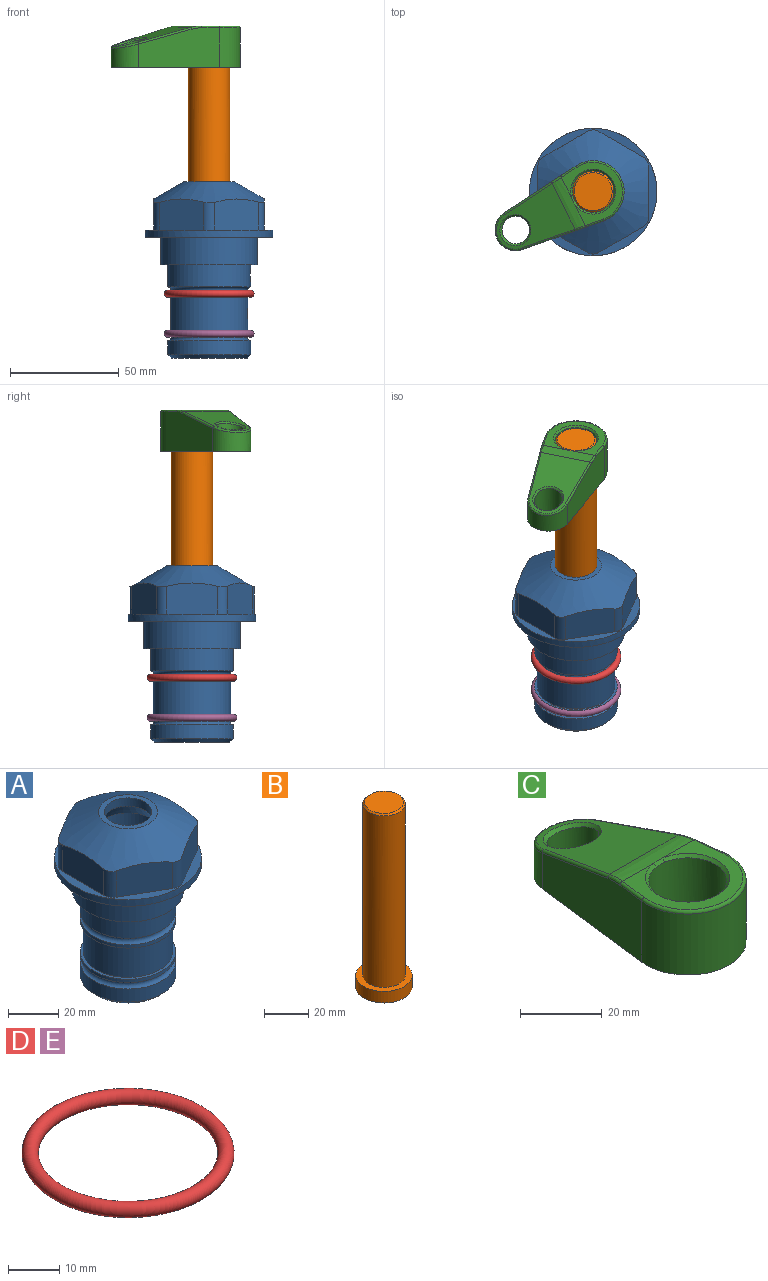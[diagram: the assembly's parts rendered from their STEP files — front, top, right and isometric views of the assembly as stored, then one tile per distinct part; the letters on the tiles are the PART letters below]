
ASSEMBLY  parts=5 mates=4
PART A: 36 faces, bbox 58.7x58.7x81 mm
  f0: cylinder r=17.78mm len=35.56mm, axis (0,0,1), area 1670.8mm2, adj f23,f24,f31
  f1: cylinder r=19.05mm len=38.1mm, axis (0,0,1), area 1191.9mm2, adj f26,f27,f30
  f2: plane 58.66x58.66mm, normal (0,0,-1), area 1150.6mm2, adj f3,f28
  f3: cylinder r=29.33mm len=58.66mm, axis (0,0,-1), area 585.1mm2, adj f2,f4
  f4: plane 58.66x58.66mm, normal (0,0,1), area 475.9mm2, adj f3,f5,f6,f7,f8,f9,f10,f11
  f5: plane 20.32x14.34mm, normal (-0.5,0.87,0), area 324.4mm2, adj f4,f15,f16,f17
  f6: plane 20.32x14.34mm, normal (0.5,0.87,0), area 324.4mm2, adj f4,f14,f15,f17
  f7: plane 23.48x14.34mm, normal (1,0,0), area 324.4mm2, adj f4,f13,f14,f17
  f8: plane 20.32x14.34mm, normal (0.5,-0.87,0), area 324.4mm2, adj f4,f12,f13,f17
  f9: plane 20.32x14.34mm, normal (-0.5,-0.87,0), area 324.4mm2, adj f4,f11,f12,f17
  f10: plane 23.48x14.34mm, normal (-1,0,0), area 324.4mm2, adj f4,f11,f16,f17
  f11: cylinder r=5.08mm len=12.85mm, axis (0,0,-1), area 67.2mm2, adj f4,f9,f10,f17
  f12: cylinder r=5.08mm len=12.85mm, axis (0,0,-1), area 67.2mm2, adj f4,f8,f9,f17
  f13: cylinder r=5.08mm len=12.85mm, axis (0,0,-1), area 67.2mm2, adj f4,f7,f8,f17
  f14: cylinder r=5.08mm len=12.85mm, axis (0,0,-1), area 67.2mm2, adj f4,f6,f7,f17
  f15: cylinder r=5.08mm len=12.85mm, axis (0,0,-1), area 67.2mm2, adj f4,f5,f6,f17
  f16: cylinder r=5.08mm len=12.85mm, axis (0,0,-1), area 67.2mm2, adj f4,f5,f10,f17
  f17: cone r=11.73mm half-angle=60deg, axis (0,0,-1), area 2071.8mm2, adj f5,f6,f7,f8,f9,f10,f11,f12
  f18: plane 23.46x23.46mm, normal (0,0,1), area 147.4mm2, adj f17,f35
  f19: plane 34.93x34.93mm, normal (0,0,-1), area 958mm2, adj f29
  f20: cylinder r=19.05mm len=38.1mm, axis (0,0,1), area 760.1mm2, adj f21,f29
  f21: torus R=19.05mm, axis (0,0,1), area 565.3mm2, adj f20,f22
  f22: cylinder r=19.05mm len=38.1mm, axis (0,0,1), area 190mm2, adj f21,f23
  f23: plane 38.1x38.1mm, normal (0,0,1), area 146.9mm2, adj f0,f22
  f24: plane 38.1x38.1mm, normal (0,0,-1), area 146.9mm2, adj f0,f25
  f25: cylinder r=19.05mm len=38.1mm, axis (0,0,1), area 190mm2, adj f24,f26
  f26: torus R=19.05mm, axis (0,0,1), area 565.3mm2, adj f1,f25
  f27: plane 44.45x44.45mm, normal (0,0,-1), area 411.7mm2, adj f1,f28
  f28: cylinder r=22.23mm len=44.45mm, axis (0,0,1), area 1773.5mm2, adj f2,f27
  f29: cone r=19.05mm half-angle=45deg, axis (0,0,1), area 257.5mm2, adj f19,f20
  f30: cylinder r=3.17mm len=6.75mm, axis (-1,0,0), area 128mm2, adj f1,f33
  f31: cylinder r=3.17mm len=6.35mm, axis (-1,0,0), area 102.5mm2, adj f0,f33
  f32: plane 25.4x25.4mm, normal (0,0,1), area 506.7mm2, adj f33
  f33: cylinder r=12.7mm len=66.42mm, axis (0,0,-1), area 5236.2mm2, adj f30,f31,f32,f34
  f34: cone r=9.53mm half-angle=30deg, axis (0,0,-1), area 443.4mm2, adj f33,f35
  f35: cylinder r=9.53mm len=19.05mm, axis (0,0,-1), area 240.9mm2, adj f18,f34
PART B: 6 faces, bbox 25.4x25.4x101.6 mm
  f0: plane 17.46x17.46mm, normal (0,0,1), area 239.5mm2, adj f5
  f1: plane 25.4x25.4mm, normal (0,0,-1), area 506.7mm2, adj f2
  f2: cylinder r=12.7mm len=25.4mm, axis (0,0,1), area 506.7mm2, adj f1,f3
  f3: plane 25.4x25.4mm, normal (0,0,1), area 221.7mm2, adj f2,f4
  f4: cylinder r=9.53mm len=94.46mm, axis (0,0,1), area 5653mm2, adj f3,f5
  f5: cone r=8.73mm half-angle=45deg, axis (0,0,-1), area 64.4mm2, adj f0,f4
PART C: 31 faces, bbox 31.7x65.5x19.8 mm
  f0: plane 39.12x18.26mm, normal (0.99,0.12,0), area 612.2mm2, adj f1,f4,f7,f11,f13,f15
  f1: cylinder r=9.53mm len=18.91mm, axis (0,0,-1), area 296.1mm2, adj f0,f2,f7,f17
  f2: plane 39.12x18.26mm, normal (-0.99,0.12,0), area 612.2mm2, adj f1,f4,f7,f12,f14,f16
  f3: cylinder r=6.35mm len=12.7mm, axis (0,0,-1), area 362.4mm2, adj f7,f18
  f4: cylinder r=14.29mm len=28.58mm, axis (0,0,-1), area 882.2mm2, adj f0,f2,f7,f10
  f5: cylinder r=9.53mm len=19.05mm, axis (0,0,-1), area 1092.6mm2, adj f7,f19,f20
  f6: plane 26.99x23.69mm, normal (0,0,1), area 216.2mm2, adj f9,f10,f11,f12,f19
  f7: plane 63.5x28.58mm, normal (0,0,-1), area 661.8mm2, adj f0,f1,f2,f3,f4,f5,f22,f23
  f8: plane 33.52x23.6mm, normal (0,0.26,0.97), area 486mm2, adj f9,f15,f16,f17,f18
  f9: cylinder r=19.05mm len=24.72mm, axis (1,0,0), area 120.4mm2, adj f6,f8,f13,f14,f20
  f10: torus R=13.49mm, axis (0,0,1), area 59mm2, adj f4,f6,f11,f12
  f11: cylinder r=0.79mm len=8.67mm, axis (0.12,-0.99,0), area 10.8mm2, adj f0,f6,f10,f13
  f12: cylinder r=0.79mm len=8.67mm, axis (0.12,0.99,0), area 10.8mm2, adj f2,f6,f10,f14
  f13: bspline ~4.95x1.42mm, area 6.1mm2, adj f0,f9,f11,f15
  f14: bspline ~4.95x1.42mm, area 6.1mm2, adj f2,f9,f12,f16
  f15: cylinder r=0.79mm len=25.95mm, axis (0.12,-0.96,0.26), area 32.9mm2, adj f0,f8,f13,f17
  f16: cylinder r=0.79mm len=25.95mm, axis (0.12,0.96,-0.26), area 32.9mm2, adj f2,f8,f14,f17
  f17: bspline ~18.91x8.38mm, area 30mm2, adj f1,f8,f15,f16
  f18: bspline ~14.29x14.29mm, area 48.3mm2, adj f3,f8
  f19: cone r=9.53mm half-angle=45deg, axis (0,0,1), area 66.5mm2, adj f5,f6,f20
  f20: bspline ~3.22x0.96mm, area 3.5mm2, adj f5,f9,f19
  f21: plane 2.75x2.72mm, normal (0,0,-1), area 2.9mm2, adj f23,f25,f28
  f22: plane 23.05x15.88mm, normal (-0.99,-0.12,0), area 323.6mm2, adj f7,f25,f26,f27,f28,f29
  f23: plane 23.05x15.88mm, normal (0.99,-0.12,0), area 323.6mm2, adj f7,f21,f25,f27,f28,f30
  f24: cylinder r=9.53mm len=10.69mm, axis (0,0,-1), area 114.7mm2, adj f7,f27,f29,f30
  f25: cylinder r=12.7mm len=20.59mm, axis (0,0,-1), area 381.1mm2, adj f7,f21,f22,f23,f26,f28
  f26: plane 2.75x2.72mm, normal (0,0,-1), area 2.9mm2, adj f22,f25,f28
  f27: plane 19.72x18.37mm, normal (0,-0.26,-0.97), area 291.8mm2, adj f22,f23,f24,f28,f29,f30
  f28: cylinder r=15.88mm len=19.92mm, axis (1,0,0), area 54.8mm2, adj f21,f22,f23,f25,f26,f27
  f29: cylinder r=1.59mm len=11mm, axis (0,0,-1), area 34.7mm2, adj f7,f22,f24,f27
  f30: cylinder r=1.59mm len=11mm, axis (0,0,-1), area 34.7mm2, adj f7,f23,f24,f27
PART D: 1 faces, bbox 44.7x44.7x3.2 mm
  f0: torus R=19.05mm, axis (0,0,1), area 1193.9mm2
PART E: same geometry as D
PLACE A at identity fixed
PLACE B rot(axis=(0,0,1),116.3deg) t=(0,0,32.79)mm
PLACE C rot(axis=(0,0,1),116.3deg) t=(0,0,33.58)mm
PLACE D t=(0,0,-1.59)mm
PLACE E t=(0,0,-20)mm
MATE fastened E.f0 <-> A.f0  axis (0,0,1) through (0,0,-44.51)mm
MATE fastened C.f4 <-> B.f2  axis (0,0,1) through (0,0,96.29)mm
MATE cylindrical A.f0 <-> B.f2  axis (0,0,1) through (0,0,-35.31)mm
MATE fastened D.f0 <-> A.f0  axis (0,0,1) through (0,0,-26.1)mm
